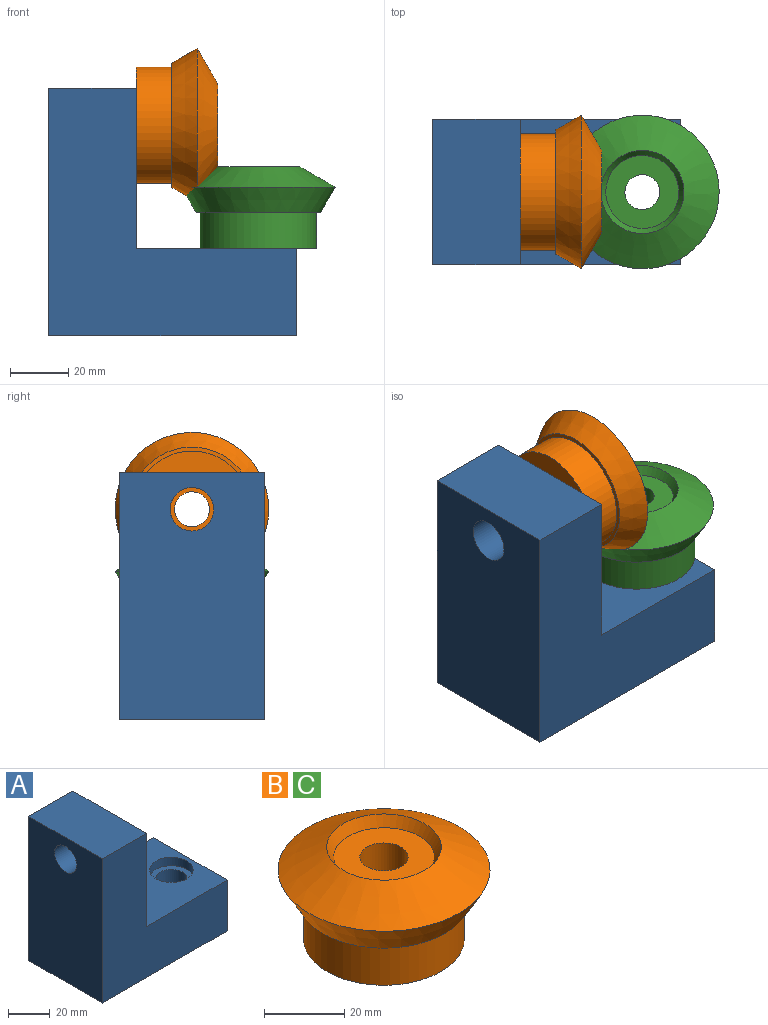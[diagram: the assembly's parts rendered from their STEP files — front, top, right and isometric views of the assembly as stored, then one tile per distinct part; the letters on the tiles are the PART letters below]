
ASSEMBLY  parts=3 mates=2
PART A: 14 faces, bbox 85x50x85 mm
  f0: plane 85x85mm, normal (0,-1,0), area 4200mm2, adj f2,f3,f4,f5,f6,f7
  f1: plane 85x85mm, normal (0,1,0), area 4200mm2, adj f2,f3,f4,f5,f6,f7
  f2: plane 50x30mm, normal (0,0,1), area 1500mm2, adj f0,f1,f5,f7
  f3: plane 50x30mm, normal (1,0,0), area 1500mm2, adj f0,f1,f4,f6
  f4: plane 85x50mm, normal (0,0,-1), area 3903.6mm2, adj f0,f1,f3,f5,f8
  f5: plane 85x50mm, normal (-1,0,0), area 4073.3mm2, adj f0,f1,f2,f4,f13
  f6: plane 55x50mm, normal (0,0,1), area 2403.6mm2, adj f0,f1,f3,f7,f11
  f7: plane 55x50mm, normal (1,0,0), area 2573.3mm2, adj f0,f1,f2,f6,f13
  f8: cylinder r=10.5mm len=21mm, axis (0,0,-1), area 329.9mm2, adj f4,f9
  f9: plane 21x21mm, normal (0,0,-1), area 169.6mm2, adj f8,f10
  f10: cylinder r=7.5mm len=20mm, axis (0,0,-1), area 942.5mm2, adj f9,f12
  f11: cylinder r=10.5mm len=21mm, axis (0,0,1), area 329.9mm2, adj f6,f12
  f12: plane 21x21mm, normal (0,0,1), area 169.6mm2, adj f10,f11
  f13: cylinder r=7.5mm len=30mm, axis (1,0,0), area 1413.7mm2, adj f5,f7
PART B: 8 faces, bbox 52.8x52.8x28 mm
  f0: cylinder r=6mm len=25mm, axis (0,0,-1), area 942.5mm2, adj f1,f7
  f1: plane 25.09x25.09mm, normal (0,0,1), area 381.2mm2, adj f0,f2
  f2: cone r=14.28mm half-angle=30deg, axis (0,0,1), area 291.9mm2, adj f1,f3
  f3: cone r=26.4mm half-angle=60deg, axis (0,0,-1), area 1789mm2, adj f2,f4
  f4: cone r=21.38mm half-angle=30deg, axis (0,0,1), area 1507.8mm2, adj f3,f5
  f5: plane 42.75x42.75mm, normal (0,0,-1), area 179mm2, adj f4,f6
  f6: cylinder r=20mm len=40mm, axis (0,0,-1), area 1545.7mm2, adj f5,f7
  f7: plane 40x40mm, normal (0,0,-1), area 1143.5mm2, adj f0,f6
PART C: same geometry as B
PLACE A t=(-8.24,-4.1,6.67)mm fixed
PLACE B rot(axis=(-0.25,0.94,-0.25),93.8deg) t=(21.76,-4.1,-6.05)mm
PLACE C rot(axis=(0,0,1),11.8deg) t=(63.76,-4.1,-48.33)mm
MATE revolute C.f0 <-> A.f11  axis (0,0,-1) through (63.76,-4.1,-48.33)mm
MATE revolute B.f0 <-> A.f13  axis (-1,0,0) through (21.76,-4.1,-6.05)mm
